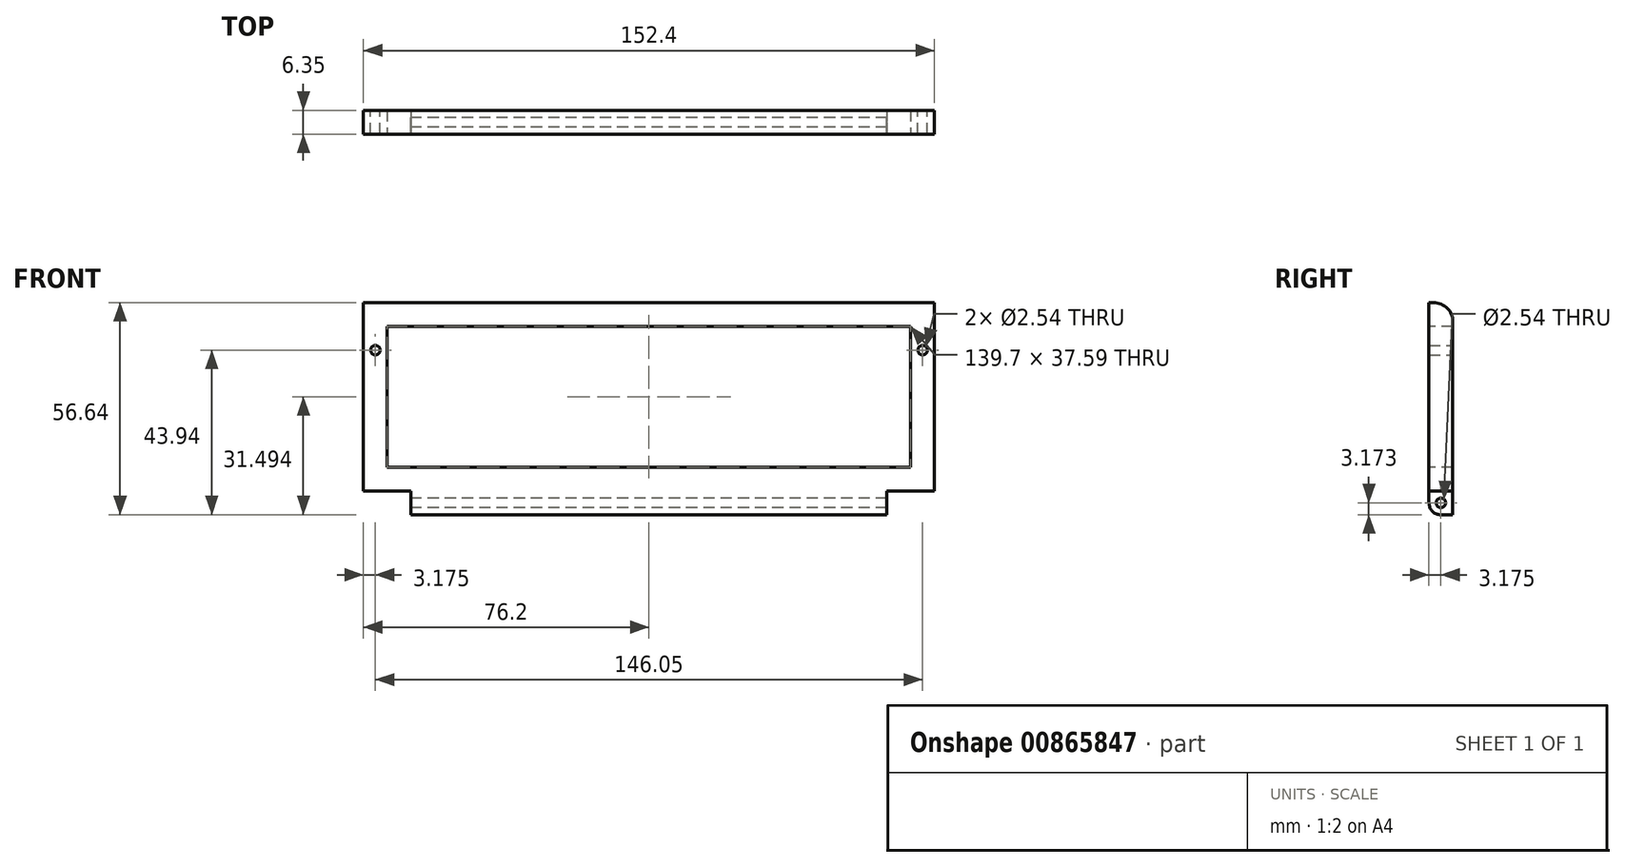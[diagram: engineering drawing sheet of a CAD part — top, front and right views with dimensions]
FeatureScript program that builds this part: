
annotation { "Feature Type Name" : "Feature", "Feature Type Description" : "" }
export const myFeature = defineFeature(function(context is Context, id is Id, definition is map)
    precondition{}
    {
        {
            var Q0;
            Q0=qCreatedBy(makeId("Front.planeOp"),FACE);
            var sketch = newSketch(context, id + "F0", { "sketchPlane" : qUnion([Q0])});
            skLineSegment(sketch, "E0.bottom", {"start": v(0, 0) * mm, "end": v(152.4, 0) * mm});
            skLineSegment(sketch, "E0.top", {"start": v(12.7, -56.64) * mm, "end": v(139.7, -56.64) * mm});
            skLineSegment(sketch, "E0.left", {"start": v(0, 0) * mm, "end": v(0, -50.3) * mm});
            skLineSegment(sketch, "E0.right", {"start": v(152.4, 0) * mm, "end": v(152.4, -50.3) * mm});
            skLineSegment(sketch, "E1.top", {"start": v(0, -50.3) * mm, "end": v(12.7, -50.3) * mm});
            skLineSegment(sketch, "E1.right", {"start": v(12.7, -56.64) * mm, "end": v(12.7, -50.3) * mm});
            skLineSegment(sketch, "E2.top", {"start": v(152.4, -50.3) * mm, "end": v(139.7, -50.3) * mm});
            skLineSegment(sketch, "E2.right", {"start": v(139.7, -56.64) * mm, "end": v(139.7, -50.3) * mm});
            skLineSegment(sketch, "E3.0", {"start": v(146.05, -43.94) * mm, "end": v(139.7, -43.94) * mm});
            skLineSegment(sketch, "E3.1", {"start": v(6.35, -43.94) * mm, "end": v(12.7, -43.94) * mm});
            skLineSegment(sketch, "E3.2", {"start": v(6.35, -6.35) * mm, "end": v(6.35, -43.94) * mm});
            skLineSegment(sketch, "E3.3", {"start": v(6.35, -6.35) * mm, "end": v(146.05, -6.35) * mm});
            skLineSegment(sketch, "E3.4", {"start": v(146.05, -6.35) * mm, "end": v(146.05, -43.94) * mm});
            skLineSegment(sketch, "E4", {"start": v(12.7, -43.94) * mm, "end": v(139.7, -43.94) * mm});
            skSolve(sketch);
        }
        {
            var Q0;
            Q0=makeQuery(id+"F0.imprint","IMPRINT",FACE,{"disambiguationData":[TD([[makeQuery(id+"F0.imprint","IMPRINT",EDGE,{"derivedFrom":sQuery(id+"F0.wireOp",EDGE,"E0.bottom")}),-1.0]])]});
            extrude(context, id + "F1", {"entities" : qUnion([Q0]), "oppositeDirection" : true, "depth" : 6.35 * mm, "offsetDistance" : 25.4 * mm});
        }
        {
            var Q0;
            Q0=makeQuery(id+"F1.opExtrude","CAP_EDGE",EDGE,{"disambiguationData":[OSD([sQuery(id+"F0.wireOp",EDGE,"E0.top")])],"isStart":true});
            fillet(context, id + "F2", {"entities" : qUnion([Q0]), "radius" : 3.17 * mm, "tangentPropagation" : true, "allowEdgeOverflow" : false});
        }
        {
            var Q0;
            Q0=makeQuery(id+"F1.opExtrude","SWEPT_FACE",FACE,{"disambiguationData":[OSD([sQuery(id+"F0.wireOp",EDGE,"E1.right")])]});
            var sketch = newSketch(context, id + "F3", { "sketchPlane" : qUnion([Q0])});
            skCircle(sketch, "E5", {"center": v(-3.18, -53.47) * mm, "radius": 1.27 * mm});
            skSolve(sketch);
        }
        {
            var Q0;
            Q0 = qSketchRegion(id + "F3", true);
            extrude(context, id + "F4", {"entities" : qUnion([Q0]), "operationType" : NewBodyOperationType.REMOVE, "endBound" : BoundingType.THROUGH_ALL, "oppositeDirection" : true, "depth" : 25.4 * mm, "offsetDistance" : 25.4 * mm});
        }
        {
            var Q0;
            Q0=makeQuery(id+"F1.opExtrude","CAP_EDGE",EDGE,{"disambiguationData":[OSD([sQuery(id+"F0.wireOp",EDGE,"E0.bottom")])],"isStart":false});
            fillet(context, id + "F5", {"entities" : qUnion([Q0]), "radius" : 5.08 * mm, "tangentPropagation" : true, "allowEdgeOverflow" : false});
        }
        {
            var Q0;
            Q0=makeQuery(id+"F1.opExtrude","CAP_FACE",FACE,{"disambiguationData":[OSD([sQuery(id+"F0.wireOp",EDGE,"E0.bottom"),sQuery(id+"F0.wireOp",EDGE,"E0.top"),sQuery(id+"F0.wireOp",EDGE,"E0.left"),sQuery(id+"F0.wireOp",EDGE,"E0.right"),sQuery(id+"F0.wireOp",EDGE,"E1.top"),sQuery(id+"F0.wireOp",EDGE,"E1.right"),sQuery(id+"F0.wireOp",EDGE,"E2.top"),sQuery(id+"F0.wireOp",EDGE,"E2.right"),sQuery(id+"F0.wireOp",EDGE,"E3.0"),sQuery(id+"F0.wireOp",EDGE,"E3.1"),sQuery(id+"F0.wireOp",EDGE,"E3.2"),sQuery(id+"F0.wireOp",EDGE,"E3.3"),sQuery(id+"F0.wireOp",EDGE,"E3.4"),sQuery(id+"F0.wireOp",EDGE,"E4")])],"isStart":false});
            var sketch = newSketch(context, id + "F6", { "sketchPlane" : qUnion([Q0])});
            skLineSegment(sketch, "E6", {"start": v(-152.4, -12.7) * mm, "end": v(-146.05, -12.7) * mm, "construction": true});
            skLineSegment(sketch, "E7", {"start": v(-6.35, -12.7) * mm, "end": v(0, -12.7) * mm, "construction": true});
            skCircle(sketch, "E8", {"center": v(-149.22, -12.7) * mm, "radius": 1.27 * mm});
            skCircle(sketch, "E9", {"center": v(-3.17, -12.7) * mm, "radius": 1.27 * mm});
            skSolve(sketch);
        }
        {
            var Q0;
            Q0 = qSketchRegion(id + "F6", true);
            extrude(context, id + "F7", {"entities" : qUnion([Q0]), "operationType" : NewBodyOperationType.REMOVE, "endBound" : BoundingType.THROUGH_ALL, "oppositeDirection" : true, "depth" : 25.4 * mm, "offsetDistance" : 25.4 * mm});
        }
    });
